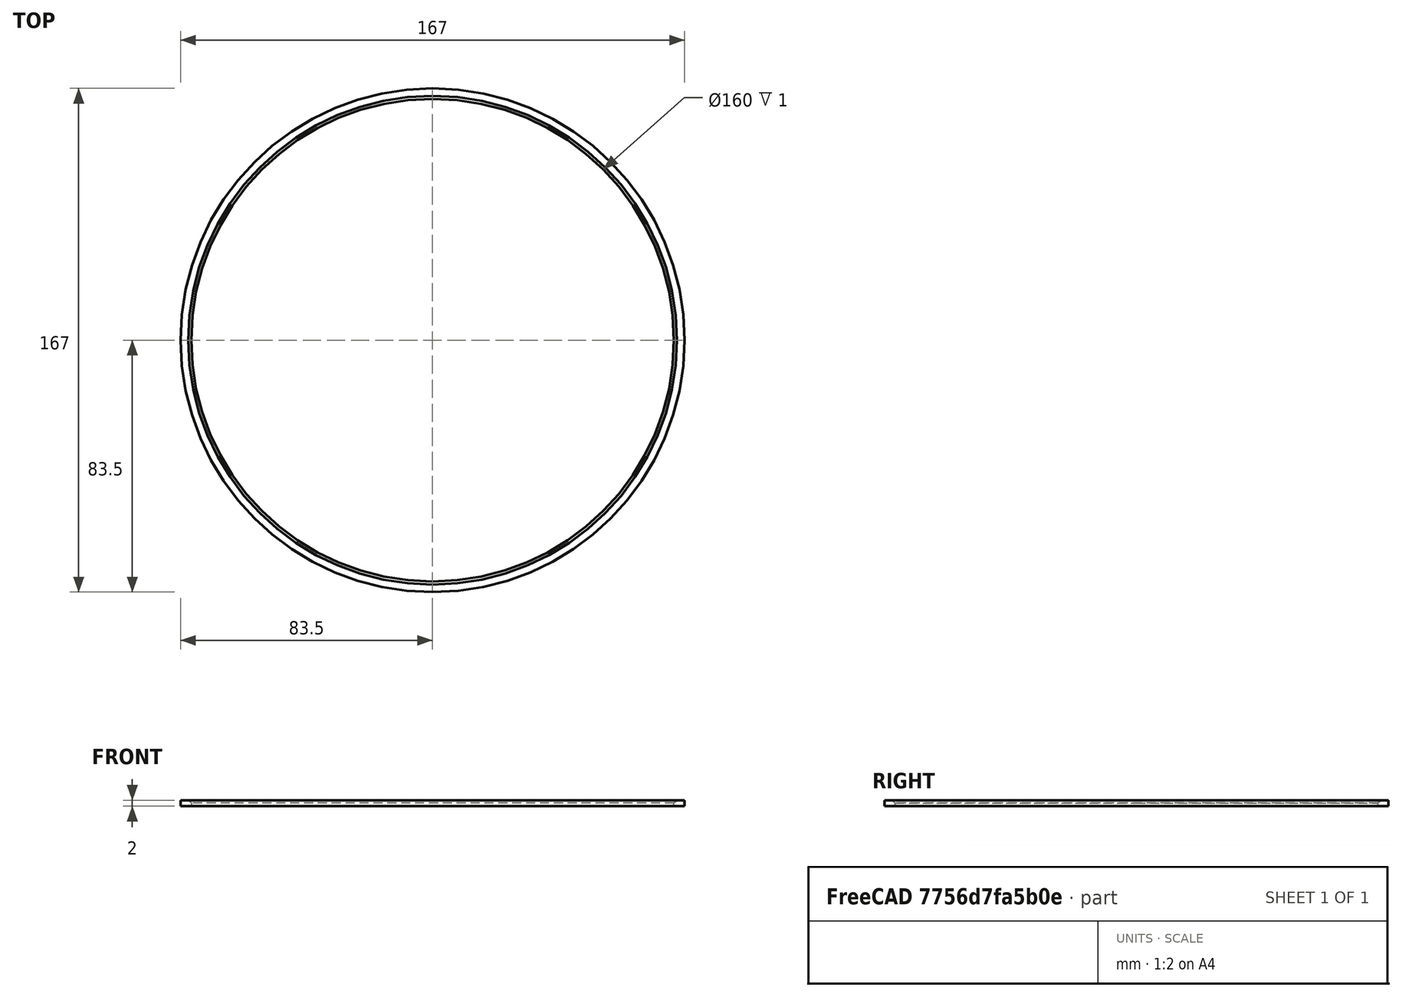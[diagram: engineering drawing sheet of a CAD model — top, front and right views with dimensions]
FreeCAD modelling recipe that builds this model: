
FCSTD DOCUMENT  (FreeCAD 0.19R24276 (Git))
Label: Gt2_ring_cover_d160_d167
License: All rights reserved
LicenseURL: http://en.wikipedia.org/wiki/All_rights_reserved
objects: Sketcher::SketchObject×1, PartDesign::Pad×1, PartDesign::Chamfer×1, PartDesign::Body×1
note: 6 computed .brp shape members not serialized (recipe doc carries the construction recipe); baked Part::Feature solids carry a one-line shape summary decoded from their .brp

FEATURE [Sketcher::SketchObject] Sketch  label="Sketch_d160_d167"
  FullyConstrained = true
  MapMode = 5
  Support = -> [XY_Plane]
  sketch-geometry (2):
    g0: Circle CenterX=0 CenterY=0 CenterZ=0 NormalX=0 NormalY=0 NormalZ=1 AngleXU=0 Radius=83.5
    g1: Circle CenterX=0 CenterY=0 CenterZ=0 NormalX=0 NormalY=0 NormalZ=1 AngleXU=0 Radius=80
  constraints (4):
    c: Coincident(g0,g-1)
    c: Coincident(g1,g0)
    c: Diameter(g0) = 167
    c: Diameter(g1) = 160
FEATURE [PartDesign::Pad] Pad  label="Pad_h2"
  Direction = (1,1,1)
  Length = 2
  Length2 = 100
  Profile = -> Sketch
  Type = 0
FEATURE [PartDesign::Chamfer] Chamfer
  Angle = 45
  Base = -> Pad [Edge6]
  BaseFeature = -> Pad
  ChamferType = 0
  FlipDirection = false
  Size = 1
  Size2 = 1
  SupportTransform = false
FEATURE [PartDesign::Body] Body
  Group = -> [Sketch,Pad,Chamfer]
  Origin = -> Origin
  Tip = -> Chamfer
